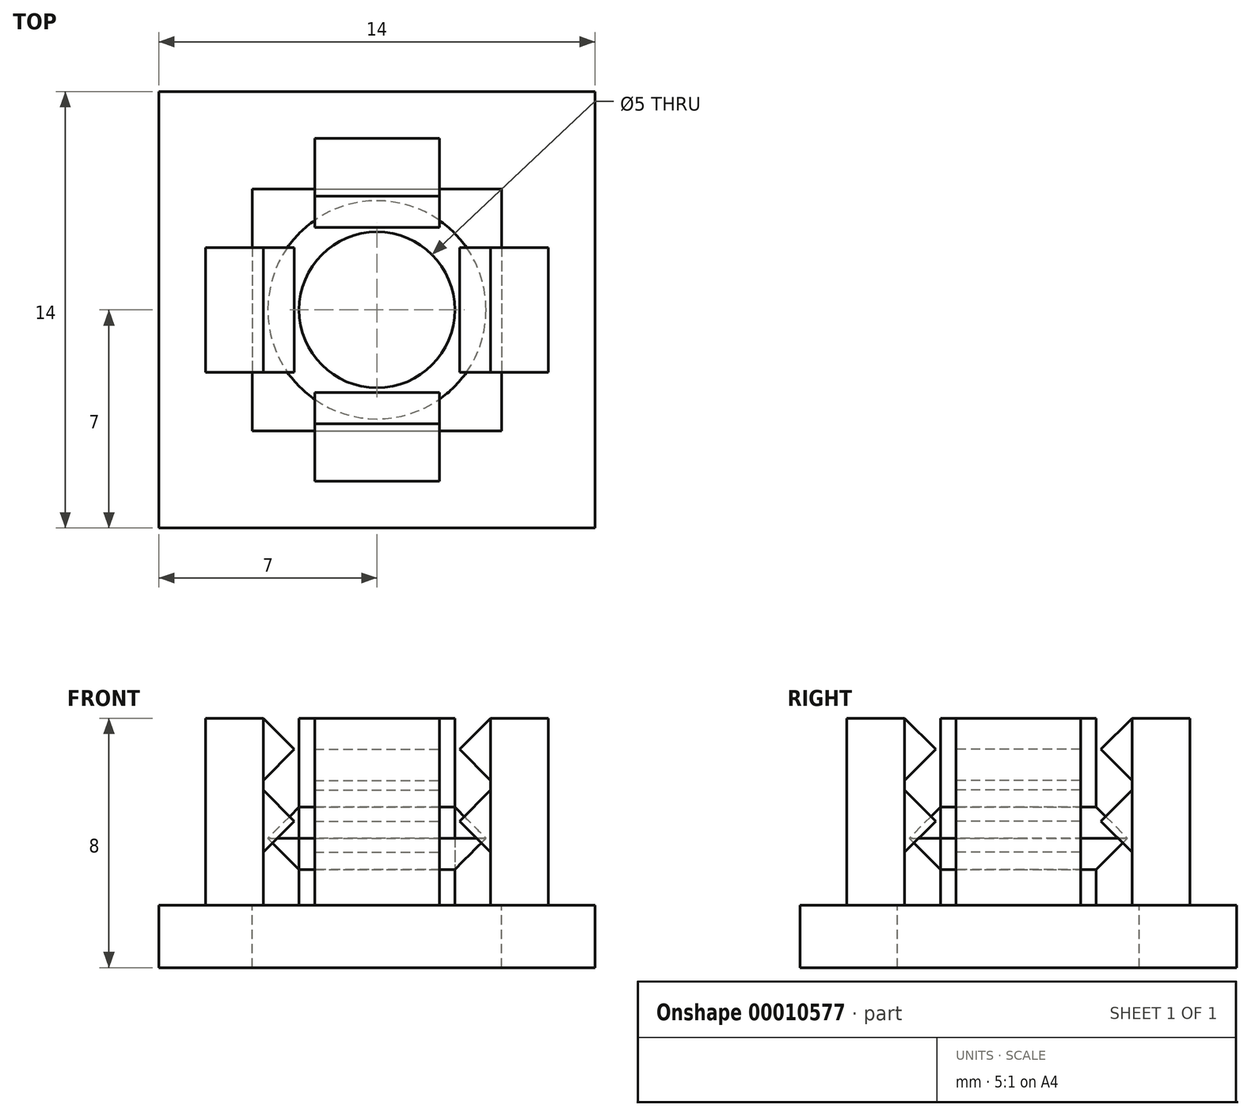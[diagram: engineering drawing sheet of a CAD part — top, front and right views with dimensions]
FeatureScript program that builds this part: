
annotation { "Feature Type Name" : "Feature", "Feature Type Description" : "" }
export const myFeature = defineFeature(function(context is Context, id is Id, definition is map)
    precondition{}
    {
        {
            var Q0;
            Q0=qCreatedBy(makeId("Top.planeOp"),FACE);
            var sketch = newSketch(context, id + "F0", { "sketchPlane" : qUnion([Q0])});
            skLineSegment(sketch, "E0.bottom", {"start": v(-4, 3.88) * mm, "end": v(4, 3.88) * mm});
            skLineSegment(sketch, "E0.top", {"start": v(-4, -3.88) * mm, "end": v(4, -3.88) * mm});
            skLineSegment(sketch, "E0.left", {"start": v(-4, 3.88) * mm, "end": v(-4, -3.88) * mm});
            skLineSegment(sketch, "E0.right", {"start": v(4, 3.88) * mm, "end": v(4, -3.88) * mm});
            skCircle(sketch, "E1", {"center": v(0, 0) * mm, "radius": 2.5 * mm});
            skCircle(sketch, "E2", {"center": v(0, 0) * mm, "radius": 3.5 * mm});
            skSolve(sketch);
        }
        {
            var Q0;
            Q0=makeQuery(id+"F0.imprint","IMPRINT",FACE,{"disambiguationData":[TD([[makeQuery(id+"F0.imprint","IMPRINT",EDGE,{"derivedFrom":sQuery(id+"F0.wireOp",EDGE,"E1")}),1.0]])]});
            extrude(context, id + "F1", {"entities" : qUnion([Q0]), "depth" : 6 * mm});
        }
        {
            var Q0;
            Q0=makeQuery(id+"F0.imprint","IMPRINT",FACE,{"disambiguationData":[TD([[makeQuery(id+"F0.imprint","IMPRINT",EDGE,{"derivedFrom":sQuery(id+"F0.wireOp",EDGE,"E1")}),-1.0]])]});
            extrude(context, id + "F2", {"entities" : qUnion([Q0]), "depth" : 3.15 * mm, "hasSecondDirection" : true, "secondDirectionOppositeDirection" : false, "secondDirectionDepth" : 1.15 * mm});
        }
        {
            var Q0;
            Q0=makeQuery(id+"F2.opExtrude","CAP_EDGE",EDGE,{"disambiguationData":[OSD([sQuery(id+"F0.wireOp",EDGE,"E2")])],"isStart":false});
            var Q1;
            Q1=makeQuery(id+"F2.opExtrude","CAP_EDGE",EDGE,{"disambiguationData":[OSD([sQuery(id+"F0.wireOp",EDGE,"E2")])],"isStart":true});
            chamfer(context, id + "F3", {"entities" : qUnion([Q0, Q1]), "width" : 1 * mm, "tangentPropagation" : true});
        }
        {
            var Q0;
            Q0=makeQuery(id+"F0.imprint","IMPRINT",FACE,{"disambiguationData":[TD([[makeQuery(id+"F0.imprint","IMPRINT",EDGE,{"derivedFrom":sQuery(id+"F0.wireOp",EDGE,"E0.bottom")}),-1.0]])]});
            var Q1;
            Q1=makeQuery(id+"F0.imprint","IMPRINT",FACE,{"disambiguationData":[TD([[makeQuery(id+"F0.imprint","IMPRINT",EDGE,{"derivedFrom":sQuery(id+"F0.wireOp",EDGE,"E1")}),-1.0]])]});
            var Q2;
            Q2=makeQuery(id+"F0.imprint","IMPRINT",FACE,{"disambiguationData":[TD([[makeQuery(id+"F0.imprint","IMPRINT",EDGE,{"derivedFrom":sQuery(id+"F0.wireOp",EDGE,"E1")}),1.0]])]});
            extrude(context, id + "F4", {"entities" : qUnion([Q0, Q1, Q2]), "oppositeDirection" : true, "depth" : 2 * mm});
        }
        {
            var Q0;
            Q0=qCreatedBy(makeId("Top.planeOp"),FACE);
            var sketch = newSketch(context, id + "F5", { "sketchPlane" : qUnion([Q0])});
            skLineSegment(sketch, "E3.bottom", {"start": v(7, 7) * mm, "end": v(-7, 7) * mm});
            skLineSegment(sketch, "E3.top", {"start": v(7, -7) * mm, "end": v(-7, -7) * mm});
            skLineSegment(sketch, "E3.left", {"start": v(7, 7) * mm, "end": v(7, -7) * mm});
            skLineSegment(sketch, "E3.right", {"start": v(-7, 7) * mm, "end": v(-7, -7) * mm});
            skLineSegment(sketch, "E4.bottom", {"start": v(-2, 5.5) * mm, "end": v(2, 5.5) * mm});
            skLineSegment(sketch, "E4.top", {"start": v(-2, 2.5) * mm, "end": v(2, 2.5) * mm});
            skLineSegment(sketch, "E4.left", {"start": v(-2, 5.5) * mm, "end": v(-2, 2.5) * mm});
            skLineSegment(sketch, "E4.right", {"start": v(2, 5.5) * mm, "end": v(2, 2.5) * mm});
            skPoint(sketch, "E5", {"position": v(0, 0) * mm});
            skCircle(sketch, "E6", {"center": v(0, 0) * mm, "radius": 2.5 * mm, "construction": true});
            skLineSegment(sketch, "E7", {"start": v(0, 0) * mm, "end": v(0, 5.5) * mm, "construction": true});
            skLineSegment(sketch, "E8.1.0", {"start": v(-2.5, -2) * mm, "end": v(-2.5, 2) * mm});
            skLineSegment(sketch, "E8.1.1", {"start": v(-5.5, -2) * mm, "end": v(-5.5, 2) * mm});
            skLineSegment(sketch, "E8.1.2", {"start": v(-5.5, 2) * mm, "end": v(-2.5, 2) * mm});
            skLineSegment(sketch, "E8.1.3", {"start": v(-5.5, -2) * mm, "end": v(-2.5, -2) * mm});
            skLineSegment(sketch, "E8.2.0", {"start": v(2, -2.5) * mm, "end": v(-2, -2.5) * mm});
            skLineSegment(sketch, "E8.2.1", {"start": v(2, -5.5) * mm, "end": v(-2, -5.5) * mm});
            skLineSegment(sketch, "E8.2.2", {"start": v(-2, -5.5) * mm, "end": v(-2, -2.5) * mm});
            skLineSegment(sketch, "E8.2.3", {"start": v(2, -5.5) * mm, "end": v(2, -2.5) * mm});
            skLineSegment(sketch, "E8.3.0", {"start": v(2.5, 2) * mm, "end": v(2.5, -2) * mm});
            skLineSegment(sketch, "E8.3.1", {"start": v(5.5, 2) * mm, "end": v(5.5, -2) * mm});
            skLineSegment(sketch, "E8.3.2", {"start": v(5.5, -2) * mm, "end": v(2.5, -2) * mm});
            skLineSegment(sketch, "E8.3.3", {"start": v(5.5, 2) * mm, "end": v(2.5, 2) * mm});
            skLineSegment(sketch, "E9", {"start": v(2, 3.65) * mm, "end": v(-2, 3.65) * mm});
            skLineSegment(sketch, "E10.1.0", {"start": v(-3.65, 2) * mm, "end": v(-3.65, -2) * mm});
            skLineSegment(sketch, "E10.2.0", {"start": v(-2, -3.65) * mm, "end": v(2, -3.65) * mm});
            skLineSegment(sketch, "E10.3.0", {"start": v(3.65, -2) * mm, "end": v(3.65, 2) * mm});
            skLineSegment(sketch, "E11", {"start": v(-2, 2.65) * mm, "end": v(2, 2.65) * mm});
            skLineSegment(sketch, "E12.1.0", {"start": v(-2.65, -2) * mm, "end": v(-2.65, 2) * mm});
            skLineSegment(sketch, "E12.2.0", {"start": v(2, -2.65) * mm, "end": v(-2, -2.65) * mm});
            skLineSegment(sketch, "E12.3.0", {"start": v(2.65, 2) * mm, "end": v(2.65, -2) * mm});
            skSolve(sketch);
        }
        {
            var Q0;
            {var subQ2=sQuery(id+"F5.wireOp",EDGE,"E4.bottom");Q0=makeQuery(id+"F5.imprint","IMPRINT",FACE,{"disambiguationData":[TD([[makeQuery(id+"F5.imprint","IMPRINT",EDGE,{"derivedFrom":subQ2}),-1.0]])]});}
            var Q1;
            {var subQ2=sQuery(id+"F5.wireOp",EDGE,"E8.3.1");Q1=makeQuery(id+"F5.imprint","IMPRINT",FACE,{"disambiguationData":[TD([[makeQuery(id+"F5.imprint","IMPRINT",EDGE,{"derivedFrom":subQ2}),-1.0]])]});}
            var Q2;
            {var subQ2=sQuery(id+"F5.wireOp",EDGE,"E8.2.1");Q2=makeQuery(id+"F5.imprint","IMPRINT",FACE,{"disambiguationData":[TD([[makeQuery(id+"F5.imprint","IMPRINT",EDGE,{"derivedFrom":subQ2}),-1.0]])]});}
            var Q3;
            {var subQ2=sQuery(id+"F5.wireOp",EDGE,"E8.1.1");Q3=makeQuery(id+"F5.imprint","IMPRINT",FACE,{"disambiguationData":[TD([[makeQuery(id+"F5.imprint","IMPRINT",EDGE,{"derivedFrom":subQ2}),-1.0]])]});}
            extrude(context, id + "F6", {"entities" : qUnion([Q0, Q1, Q2, Q3]), "depth" : 6 * mm});
        }
        {
            var Q0;
            {var subQ1=sQuery(id+"F5.wireOp",EDGE,"E10.1.0");Q0=makeQuery(id+"F5.imprint","IMPRINT",FACE,{"disambiguationData":[TD([[makeQuery(id+"F5.imprint","IMPRINT",EDGE,{"derivedFrom":subQ1}),1.0]])]});}
            var Q1;
            {var subQ1=sQuery(id+"F5.wireOp",EDGE,"E9");Q1=makeQuery(id+"F5.imprint","IMPRINT",FACE,{"disambiguationData":[TD([[makeQuery(id+"F5.imprint","IMPRINT",EDGE,{"derivedFrom":subQ1}),1.0]])]});}
            var Q2;
            {var subQ1=sQuery(id+"F5.wireOp",EDGE,"E10.3.0");Q2=makeQuery(id+"F5.imprint","IMPRINT",FACE,{"disambiguationData":[TD([[makeQuery(id+"F5.imprint","IMPRINT",EDGE,{"derivedFrom":subQ1}),1.0]])]});}
            var Q3;
            {var subQ1=sQuery(id+"F5.wireOp",EDGE,"E10.2.0");Q3=makeQuery(id+"F5.imprint","IMPRINT",FACE,{"disambiguationData":[TD([[makeQuery(id+"F5.imprint","IMPRINT",EDGE,{"derivedFrom":subQ1}),1.0]])]});}
            extrude(context, id + "F7", {"entities" : qUnion([Q0, Q1, Q2, Q3]), "depth" : 3.7 * mm, "hasSecondDirection" : true, "secondDirectionOppositeDirection" : false, "secondDirectionDepth" : 1.7 * mm});
        }
        {
            var Q0;
            Q0=makeQuery(id+"F7.opExtrude","CAP_EDGE",EDGE,{"disambiguationData":[OSD([sQuery(id+"F5.wireOp",EDGE,"E12.1.0")])],"isStart":false});
            var Q1;
            Q1=makeQuery(id+"F7.opExtrude","CAP_EDGE",EDGE,{"disambiguationData":[OSD([sQuery(id+"F5.wireOp",EDGE,"E11")])],"isStart":false});
            var Q2;
            Q2=makeQuery(id+"F7.opExtrude","CAP_EDGE",EDGE,{"disambiguationData":[OSD([sQuery(id+"F5.wireOp",EDGE,"E11")])],"isStart":true});
            var Q3;
            Q3=makeQuery(id+"F7.opExtrude","CAP_EDGE",EDGE,{"disambiguationData":[OSD([sQuery(id+"F5.wireOp",EDGE,"E12.1.0")])],"isStart":true});
            var Q4;
            Q4=makeQuery(id+"F7.opExtrude","CAP_EDGE",EDGE,{"disambiguationData":[OSD([sQuery(id+"F5.wireOp",EDGE,"E12.3.0")])],"isStart":true});
            var Q5;
            Q5=makeQuery(id+"F7.opExtrude","CAP_EDGE",EDGE,{"disambiguationData":[OSD([sQuery(id+"F5.wireOp",EDGE,"E12.3.0")])],"isStart":false});
            var Q6;
            Q6=makeQuery(id+"F7.opExtrude","CAP_EDGE",EDGE,{"disambiguationData":[OSD([sQuery(id+"F5.wireOp",EDGE,"E12.2.0")])],"isStart":true});
            var Q7;
            Q7=makeQuery(id+"F7.opExtrude","CAP_EDGE",EDGE,{"disambiguationData":[OSD([sQuery(id+"F5.wireOp",EDGE,"E12.2.0")])],"isStart":false});
            chamfer(context, id + "F8", {"entities" : qUnion([Q0, Q1, Q2, Q3, Q4, Q5, Q6, Q7]), "width" : 1 * mm, "tangentPropagation" : true});
        }
        {
            var Q0;
            {var subQ1=sQuery(id+"F5.wireOp",EDGE,"E10.1.0");Q0=makeQuery(id+"F5.imprint","IMPRINT",FACE,{"disambiguationData":[TD([[makeQuery(id+"F5.imprint","IMPRINT",EDGE,{"derivedFrom":subQ1}),1.0]])]});}
            var Q1;
            {var subQ1=sQuery(id+"F5.wireOp",EDGE,"E10.3.0");Q1=makeQuery(id+"F5.imprint","IMPRINT",FACE,{"disambiguationData":[TD([[makeQuery(id+"F5.imprint","IMPRINT",EDGE,{"derivedFrom":subQ1}),1.0]])]});}
            var Q2;
            {var subQ1=sQuery(id+"F5.wireOp",EDGE,"E10.2.0");Q2=makeQuery(id+"F5.imprint","IMPRINT",FACE,{"disambiguationData":[TD([[makeQuery(id+"F5.imprint","IMPRINT",EDGE,{"derivedFrom":subQ1}),1.0]])]});}
            var Q3;
            {var subQ1=sQuery(id+"F5.wireOp",EDGE,"E9");Q3=makeQuery(id+"F5.imprint","IMPRINT",FACE,{"disambiguationData":[TD([[makeQuery(id+"F5.imprint","IMPRINT",EDGE,{"derivedFrom":subQ1}),1.0]])]});}
            extrude(context, id + "F9", {"entities" : qUnion([Q0, Q1, Q2, Q3]), "depth" : 6 * mm, "hasSecondDirection" : true, "secondDirectionOppositeDirection" : false, "secondDirectionDepth" : 4 * mm});
        }
        {
            var Q0;
            Q0=makeQuery(id+"F9.opExtrude","CAP_EDGE",EDGE,{"disambiguationData":[OSD([sQuery(id+"F5.wireOp",EDGE,"E12.1.0")])],"isStart":false});
            var Q1;
            Q1=makeQuery(id+"F9.opExtrude","CAP_EDGE",EDGE,{"disambiguationData":[OSD([sQuery(id+"F5.wireOp",EDGE,"E11")])],"isStart":false});
            var Q2;
            Q2=makeQuery(id+"F9.opExtrude","CAP_EDGE",EDGE,{"disambiguationData":[OSD([sQuery(id+"F5.wireOp",EDGE,"E12.3.0")])],"isStart":false});
            var Q3;
            Q3=makeQuery(id+"F9.opExtrude","CAP_EDGE",EDGE,{"disambiguationData":[OSD([sQuery(id+"F5.wireOp",EDGE,"E12.3.0")])],"isStart":true});
            var Q4;
            Q4=makeQuery(id+"F9.opExtrude","CAP_EDGE",EDGE,{"disambiguationData":[OSD([sQuery(id+"F5.wireOp",EDGE,"E11")])],"isStart":true});
            var Q5;
            Q5=makeQuery(id+"F9.opExtrude","CAP_EDGE",EDGE,{"disambiguationData":[OSD([sQuery(id+"F5.wireOp",EDGE,"E12.1.0")])],"isStart":true});
            var Q6;
            Q6=makeQuery(id+"F9.opExtrude","CAP_EDGE",EDGE,{"disambiguationData":[OSD([sQuery(id+"F5.wireOp",EDGE,"E12.2.0")])],"isStart":true});
            var Q7;
            Q7=makeQuery(id+"F9.opExtrude","CAP_EDGE",EDGE,{"disambiguationData":[OSD([sQuery(id+"F5.wireOp",EDGE,"E12.2.0")])],"isStart":false});
            chamfer(context, id + "F10", {"entities" : qUnion([Q0, Q1, Q2, Q3, Q4, Q5, Q6, Q7]), "width" : 1 * mm, "tangentPropagation" : true});
        }
        {
            var Q0;
            Q0=makeQuery(id+"F5.imprint","IMPRINT",FACE,{"disambiguationData":[TD([[makeQuery(id+"F5.imprint","IMPRINT",EDGE,{"derivedFrom":sQuery(id+"F5.wireOp",EDGE,"E3.bottom")}),1.0]])]});
            var Q1;
            {var subQ1=sQuery(id+"F5.wireOp",EDGE,"E10.2.0");Q1=makeQuery(id+"F5.imprint","IMPRINT",FACE,{"disambiguationData":[TD([[makeQuery(id+"F5.imprint","IMPRINT",EDGE,{"derivedFrom":subQ1}),1.0]])]});}
            var Q2;
            {var subQ2=sQuery(id+"F5.wireOp",EDGE,"E8.2.0");Q2=makeQuery(id+"F5.imprint","IMPRINT",FACE,{"disambiguationData":[TD([[makeQuery(id+"F5.imprint","IMPRINT",EDGE,{"derivedFrom":subQ2}),1.0]])]});}
            var Q3;
            {var subQ1=sQuery(id+"F5.wireOp",EDGE,"E10.1.0");Q3=makeQuery(id+"F5.imprint","IMPRINT",FACE,{"disambiguationData":[TD([[makeQuery(id+"F5.imprint","IMPRINT",EDGE,{"derivedFrom":subQ1}),1.0]])]});}
            var Q4;
            {var subQ2=sQuery(id+"F5.wireOp",EDGE,"E8.1.0");Q4=makeQuery(id+"F5.imprint","IMPRINT",FACE,{"disambiguationData":[TD([[makeQuery(id+"F5.imprint","IMPRINT",EDGE,{"derivedFrom":subQ2}),1.0]])]});}
            var Q5;
            {var subQ2=sQuery(id+"F5.wireOp",EDGE,"E8.3.0");Q5=makeQuery(id+"F5.imprint","IMPRINT",FACE,{"disambiguationData":[TD([[makeQuery(id+"F5.imprint","IMPRINT",EDGE,{"derivedFrom":subQ2}),1.0]])]});}
            var Q6;
            {var subQ1=sQuery(id+"F5.wireOp",EDGE,"E10.3.0");Q6=makeQuery(id+"F5.imprint","IMPRINT",FACE,{"disambiguationData":[TD([[makeQuery(id+"F5.imprint","IMPRINT",EDGE,{"derivedFrom":subQ1}),1.0]])]});}
            var Q7;
            {var subQ2=sQuery(id+"F5.wireOp",EDGE,"E4.top");Q7=makeQuery(id+"F5.imprint","IMPRINT",FACE,{"disambiguationData":[TD([[makeQuery(id+"F5.imprint","IMPRINT",EDGE,{"derivedFrom":subQ2}),1.0]])]});}
            var Q8;
            {var subQ1=sQuery(id+"F5.wireOp",EDGE,"E9");Q8=makeQuery(id+"F5.imprint","IMPRINT",FACE,{"disambiguationData":[TD([[makeQuery(id+"F5.imprint","IMPRINT",EDGE,{"derivedFrom":subQ1}),1.0]])]});}
            var Q9;
            {var subQ2=sQuery(id+"F5.wireOp",EDGE,"E8.1.1");Q9=makeQuery(id+"F5.imprint","IMPRINT",FACE,{"disambiguationData":[TD([[makeQuery(id+"F5.imprint","IMPRINT",EDGE,{"derivedFrom":subQ2}),-1.0]])]});}
            var Q10;
            {var subQ2=sQuery(id+"F5.wireOp",EDGE,"E8.3.1");Q10=makeQuery(id+"F5.imprint","IMPRINT",FACE,{"disambiguationData":[TD([[makeQuery(id+"F5.imprint","IMPRINT",EDGE,{"derivedFrom":subQ2}),-1.0]])]});}
            var Q11;
            {var subQ2=sQuery(id+"F5.wireOp",EDGE,"E4.bottom");Q11=makeQuery(id+"F5.imprint","IMPRINT",FACE,{"disambiguationData":[TD([[makeQuery(id+"F5.imprint","IMPRINT",EDGE,{"derivedFrom":subQ2}),-1.0]])]});}
            var Q12;
            {var subQ2=sQuery(id+"F5.wireOp",EDGE,"E8.2.1");Q12=makeQuery(id+"F5.imprint","IMPRINT",FACE,{"disambiguationData":[TD([[makeQuery(id+"F5.imprint","IMPRINT",EDGE,{"derivedFrom":subQ2}),-1.0]])]});}
            extrude(context, id + "F11", {"entities" : qUnion([Q0, Q1, Q2, Q3, Q4, Q5, Q6, Q7, Q8, Q9, Q10, Q11, Q12]), "oppositeDirection" : true, "depth" : 2 * mm});
        }
    });
